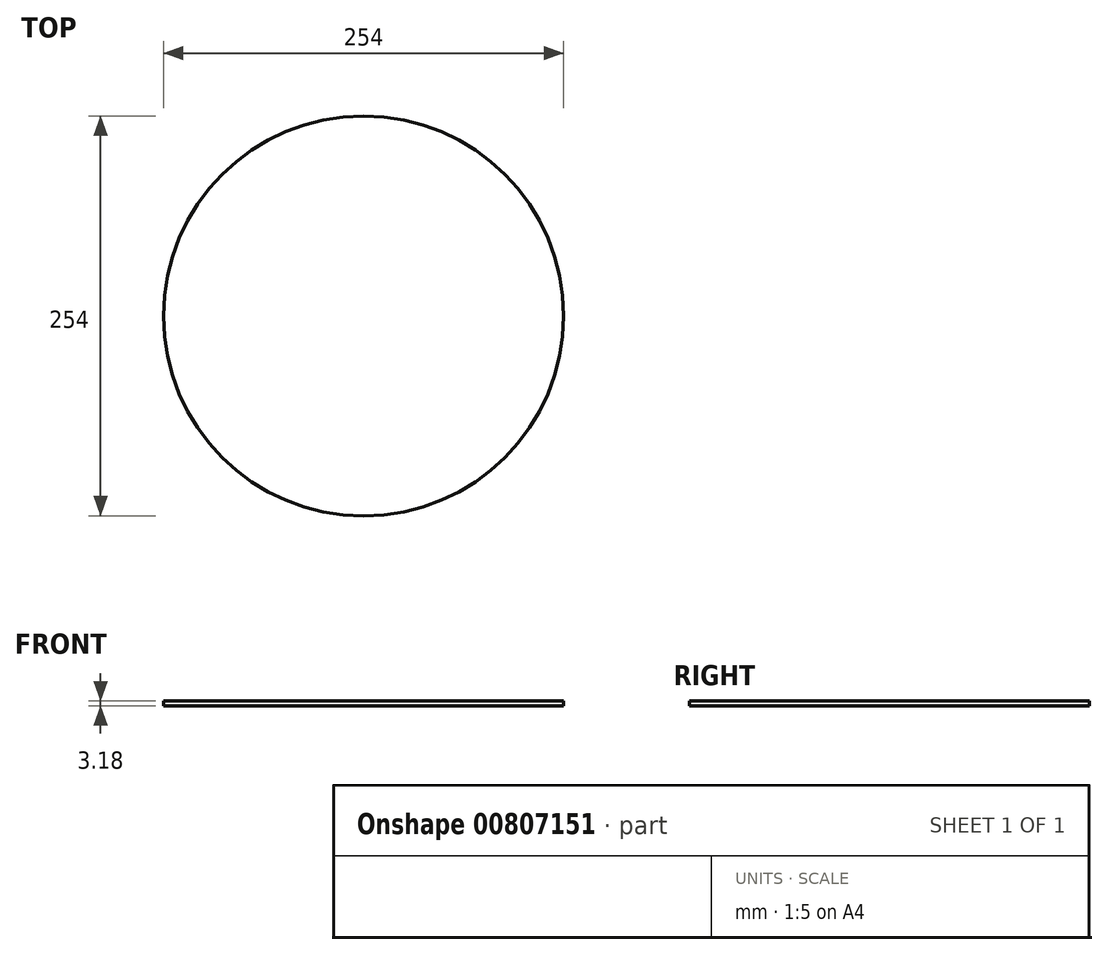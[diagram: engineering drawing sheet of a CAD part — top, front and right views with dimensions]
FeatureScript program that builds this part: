
annotation { "Feature Type Name" : "Feature", "Feature Type Description" : "" }
export const myFeature = defineFeature(function(context is Context, id is Id, definition is map)
    precondition{}
    {
        {
            var Q0;
            Q0=qCreatedBy(makeId("Top.planeOp"),FACE);
            var sketch = newSketch(context, id + "F0", { "sketchPlane" : qUnion([Q0])});
            skCircle(sketch, "E0", {"center": v(0, 0) * mm, "radius": 127 * mm});
            skSolve(sketch);
        }
        {
            var Q0;
            Q0=qSketchRegion(id+"F0",true);
            extrude(context, id + "F1", {"entities" : qUnion([Q0]), "depth" : 3.17 * mm, "offsetDistance" : 25.4 * mm});
        }
    });
